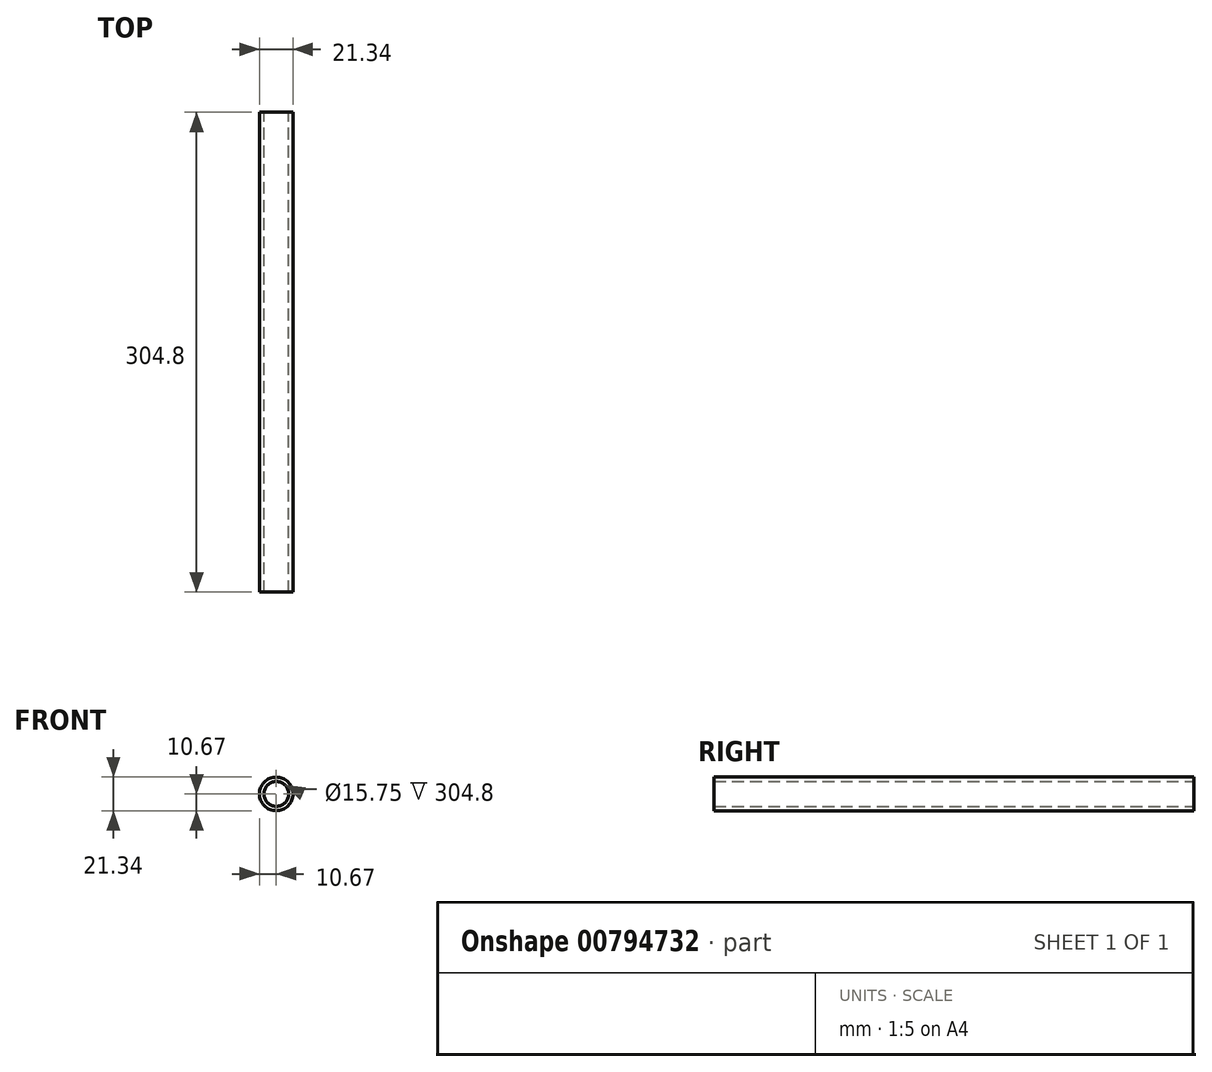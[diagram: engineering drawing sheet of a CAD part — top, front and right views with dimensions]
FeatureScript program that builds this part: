
annotation { "Feature Type Name" : "Feature", "Feature Type Description" : "" }
export const myFeature = defineFeature(function(context is Context, id is Id, definition is map)
    precondition{}
    {
        {
            var Q0;
            Q0=qCreatedBy(makeId("Front.planeOp"),FACE);
            var sketch = newSketch(context, id + "F0", { "sketchPlane" : qUnion([Q0])});
            skCircle(sketch, "E0", {"center": v(0, 0) * mm, "radius": 7.87 * mm});
            skCircle(sketch, "E1", {"center": v(0, 0) * mm, "radius": 10.67 * mm});
            skSolve(sketch);
        }
        {
            var Q0;
            Q0 = qSketchRegion(id + "F0", true);
            extrude(context, id + "F1", {"entities" : qUnion([Q0]), "depth" : 304.8 * mm, "offsetDistance" : 25.4 * mm});
        }
    });
